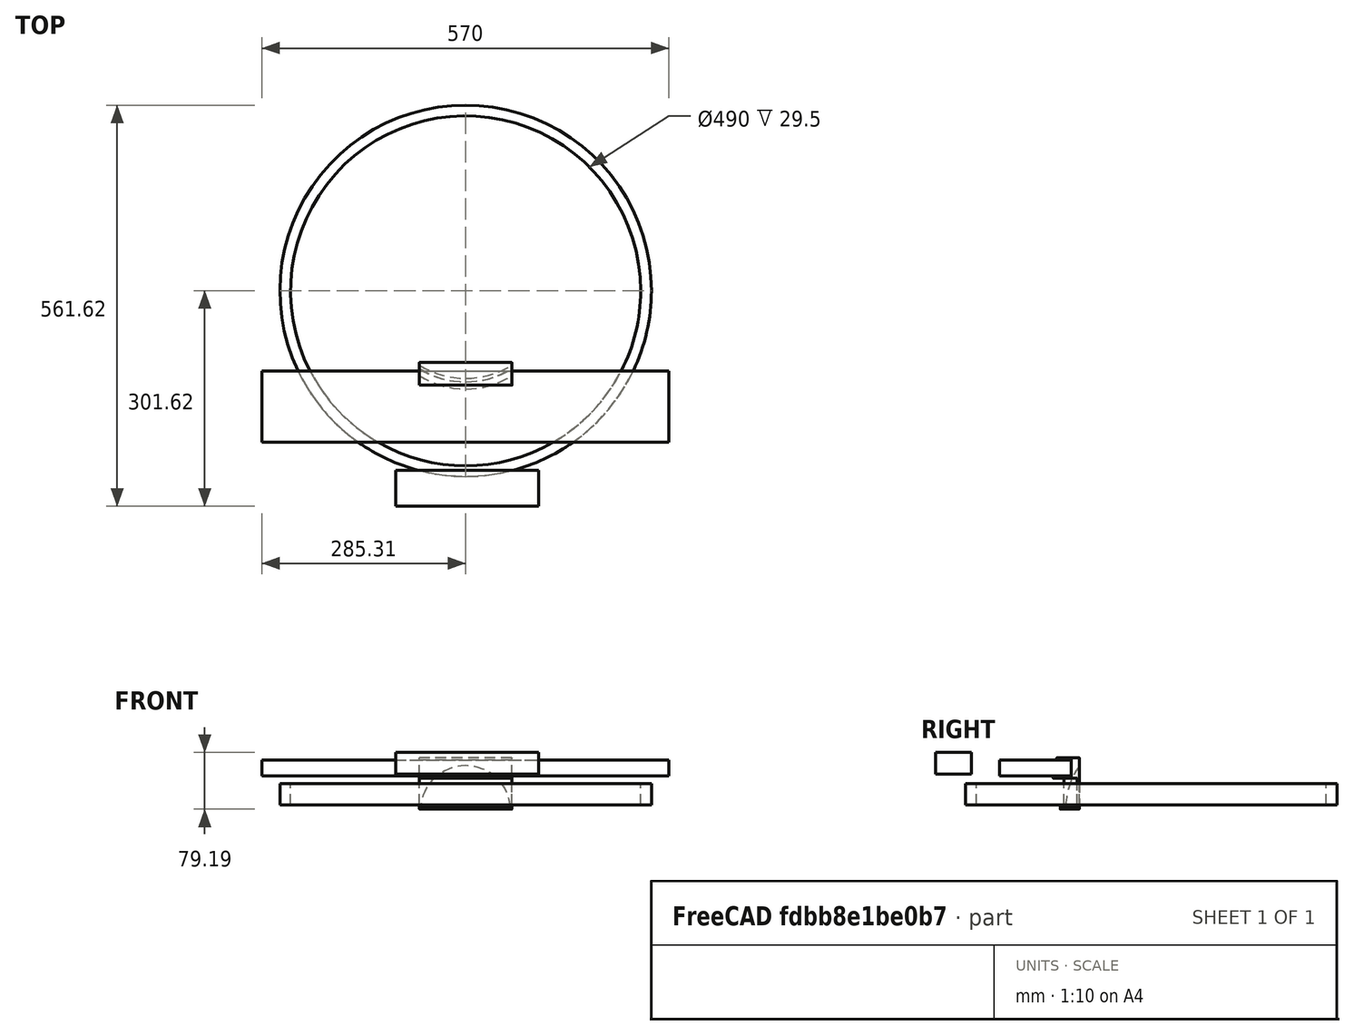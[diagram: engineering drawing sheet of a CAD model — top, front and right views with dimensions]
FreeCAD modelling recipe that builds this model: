
FCSTD DOCUMENT  (FreeCAD 0.20R29410 (Git))
Label: Бортик
License: All rights reserved
LicenseURL: http://en.wikipedia.org/wiki/All_rights_reserved
objects: Part::Cut×6, Part::Box×5, Part::FeaturePython×4, Part::Fillet×4, Part::Sphere×1, Mesh::Feature×1
note: 20 computed .brp shape members not serialized (recipe doc carries the construction recipe); baked Part::Feature solids carry a one-line shape summary decoded from their .brp

FEATURE [Part::FeaturePython] Tube  label="Бак (модель)"  # WARN: FeaturePython — macro-defined, semantics opaque (R4)
  AttacherType = Attacher::AttachEngine3D
  Height = 29.5
  InnerRadius = 245
  OuterRadius = 260
FEATURE [Part::Box] Box  label="Прямоугольник"
  AttacherType = Attacher::AttachEngine3D
  Height = 72
  Length = 130
  Placement = pos=(-65.03,-170.42,-6) rot=(0,0,1;0rad)
  Width = 70
FEATURE [Part::Sphere] Sphere  label="Сфера"
  Angle1 = -90
  Angle2 = 90
  Angle3 = 360
  AttacherType = Attacher::AttachEngine3D
  Placement = pos=(-0.01,-10.37,-8.39) rot=(0,0,1;0rad)
  Radius = 110
FEATURE [Part::Box] Box001  label="Нижняя база"
  AttacherType = Attacher::AttachEngine3D
  Height = 22.5
  Length = 570
  Placement = pos=(-285.31,-212.1,40.46) rot=(0,0,1;0rad)
  Width = 100
  expr: Height = 22.5mm
FEATURE [Part::FeaturePython] Tube001  label="Барабан001"  # WARN: FeaturePython — macro-defined, semantics opaque (R4)
  AttacherType = Attacher::AttachEngine3D
  Height = 40.5
  InnerRadius = 122.5
  OuterRadius = 250
  Placement = pos=(0,0,-3) rot=(0,0,1;0rad)
  expr: InnerRadius = 122.5mm
FEATURE [Part::Box] Box002  label="Куб"
  AttacherType = Attacher::AttachEngine3D
  Height = 30
  Length = 200
  Placement = pos=(-98.03,-301.62,43.19) rot=(0,0,1;0rad)
  Width = 50
FEATURE [Part::Box] Box003  label="Вырез 01"
  AttacherType = Attacher::AttachEngine3D
  Height = 22.5
  Length = 570
  Placement = pos=(-285.31,-232.1,44.4) rot=(0,0,1;0rad)
  Width = 100
  expr: Height = 22.5mm
FEATURE [Part::Cut] Cut  label="Бортик"
  Base = -> Box
  Tool = -> Box001
FEATURE [Part::FeaturePython] Tube002  label="Барабан002"  # WARN: FeaturePython — macro-defined, semantics opaque (R4)
  AttacherType = Attacher::AttachEngine3D
  Height = 37.5
  InnerRadius = 122.5
  OuterRadius = 250
  Placement = pos=(0,-5,-10) rot=(0,0,1;0rad)
  expr: InnerRadius = 122.5mm
FEATURE [Part::FeaturePython] Tube003  label="Барабан003"  # WARN: FeaturePython — macro-defined, semantics opaque (R4)
  AttacherType = Attacher::AttachEngine3D
  Height = 37.5
  InnerRadius = 122.5
  OuterRadius = 250
  Placement = pos=(0,-15,10) rot=(0,0,1;0rad)
  expr: InnerRadius = 122.5mm
FEATURE [Part::Box] Box004  label="Нижняя база002"
  AttacherType = Attacher::AttachEngine3D
  Height = 22.5
  Length = 570
  Placement = pos=(-285.31,-212.1,40.46) rot=(0,0,1;0rad)
  Width = 100
  expr: Height = 22.5mm
FEATURE [Part::Cut] Cut001  label="Бортик001"
  Base = -> Cut
  Tool = -> Tube001
FEATURE [Part::Cut] Cut002  label="Бортик002"
  Base = -> Cut001
  Tool = -> Tube002
FEATURE [Part::Cut] Cut003  label="Бортик003"
  Base = -> Cut002
  Tool = -> Tube003
FEATURE [Part::Cut] Cut004  label="Бортик004"
  Base = -> Cut003
  Tool = -> Box003
FEATURE [Part::Cut] Cut005  label="Бортик005"
  Base = -> Cut004
  Tool = -> Sphere
FEATURE [Part::Fillet] Fillet
  Base = -> Cut005
  Edges = 6 edges r=1: [Edge11,Edge32,Edge34,Edge36,Edge37,Edge38]
FEATURE [Part::Fillet] Fillet001
  Base = -> Fillet
  Edges = 2 edges r=0.5: [Edge11,Edge22]
FEATURE [Part::Fillet] Fillet002
  Base = -> Fillet001
  Edges = 6 edges r=0.5: [Edge10,Edge12,Edge17,Edge21,Edge30,Edge31]
FEATURE [Part::Fillet] Fillet003  label="Бортик006"
  Base = -> Fillet002
  Edges = 11 edges r=0.5: [Edge4,Edge6,Edge7,Edge8,Edge36,Edge37,Edge39,Edge44,Edge47,Edge49,Edge50]
FEATURE [Mesh::Feature] Mesh  label="Бортик006 (Meshed)"
